# Revit family: Basin-Undermount-American_Standard-Ovalyn-9482000_Series
name_source: partatom
category: Plumbing Fixtures
revit_build: Autodesk Revit 2018 (Build: 20170223_1515(x64)
units: mm (PartAtom-declared; Revit-internal decimal feet)

## family parameters
Always vertical = No
Cut with Voids When Loaded = Yes
OmniClass Number = 23.45.05.14.14
OmniClass Title = Sinks/Lavatories
Part Type = Normal
Room Calculation Point = No
Round Connector Dimension = Use Radius
Shared = Yes
Work Plane-Based = Yes

## types (1)
- 9482.000.020
    047194-0070A- Mounting Kit = Yes
    ADA Compliant = Yes
    Assembly Code = D2010310
    Basin Shape = Oval
    Bowl Depth = 4"
    Bowl Length = 13 1/4"
    Bowl Width = 16 3/4"
    CW Connection = Yes
    CWFU = 1.5
    Cold Water Connection Diameter = 1/2"
    Cold Water Connection Height = 23 1/2"
    Cold Water Connection Radius = 1/4"
    Cold Water Connection Width = 4"
    Default Elevation = 34"
    Description = Ovalyn Universal Access undercounter sink
    Faucet Hole Diameter = 1 7/16"
    Finish = Vitreous China-American Standard-020-White
    HW Connection = Yes
    HWFU = 1.5
    Height = 5 1/2"
    Hot Water Connection Diameter = 1/2"
    Hot Water Connection Height = 23 1/2"
    Hot Water Connection Radius = 1/4"
    Hot Water Connection Width = 4"
    IAPMO Compliance = Meets or Exceeds: ASME A112.19.2M for Vitreous China Fixtures, CAN/CSA B45 series, 1995 National Building Code, section 3.7,and CAN/CSA-B651-M90 and OBC 3.7.
    Installation Type = Undercounter
    Length = 15 3/4"
    Manufacturer = American Standard
    Material = Vitreous China-American Standard-020-White
    Model = 9482.000.020
    Price = Prices may vary. Please consult Manufacturer Representative for most up-to-date price list.
    Product Documentation Link = https://americanstandard.box.com
    Product Page URL = https://www.americanstandard-us.com
    Revised Date = 04/26/2022
    URL = http://www.americanstandard-us.com
    Vent Connection = No
    WFU = 2
    Waste Connection = Yes
    Waste Connection Diameter = 1 1/4"
    Waste Connection Height = 21 3/4"
    Waste Connection Radius = 5/8"
    Width = 19 1/4"

## geometry (parser evidence)
native form markers: Sweep x2
no freeform markers — native parametric forms only
